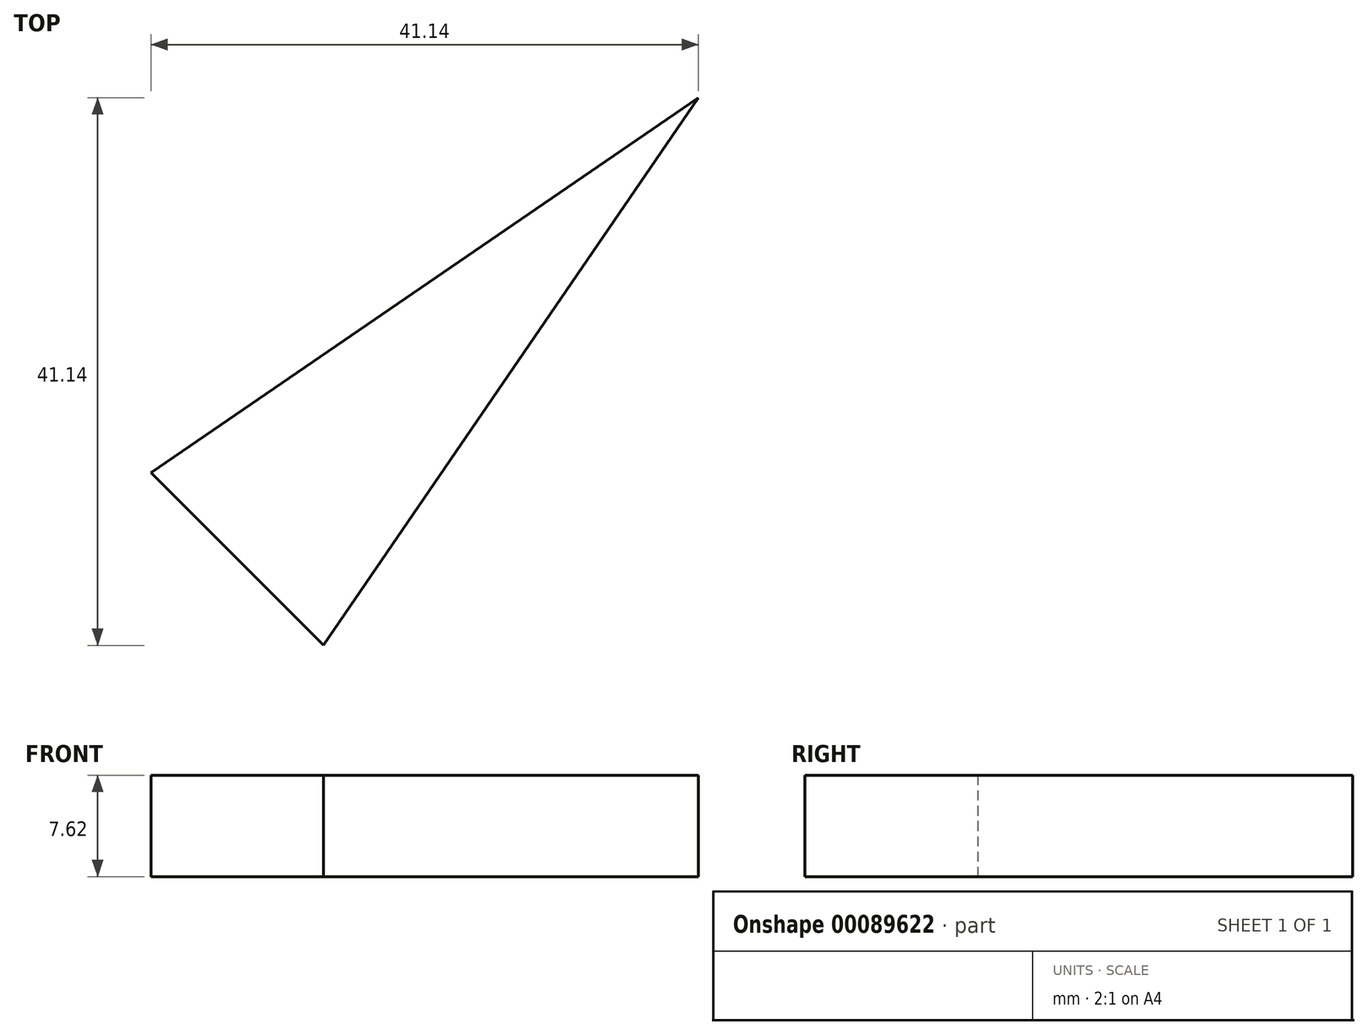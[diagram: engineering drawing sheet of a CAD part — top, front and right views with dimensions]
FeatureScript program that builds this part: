
annotation { "Feature Type Name" : "Feature", "Feature Type Description" : "" }
export const myFeature = defineFeature(function(context is Context, id is Id, definition is map)
    precondition{}
    {
        {
            var Q0;
            Q0=qCreatedBy(makeId("Top.planeOp"),FACE);
            var sketch = newSketch(context, id + "F0", { "sketchPlane" : qUnion([Q0])});
            skCircle(sketch, "E0", {"center": v(0, 0) * mm, "radius": 21.64 * mm});
            skLineSegment(sketch, "E1", {"start": v(0, 21.64) * mm, "end": v(0, -21.64) * mm});
            skLineSegment(sketch, "E2", {"start": v(0, 68.6) * mm, "end": v(0, 22.42) * mm});
            skLineSegment(sketch, "E3", {"start": v(0, 68.6) * mm, "end": v(-9.17, 19.6) * mm});
            skLineSegment(sketch, "E4", {"start": v(-9.17, 19.6) * mm, "end": v(0, 68.6) * mm});
            skLineSegment(sketch, "E5", {"start": v(9.17, 19.6) * mm, "end": v(0, 68.6) * mm});
            skLineSegment(sketch, "E6", {"start": v(-9.17, 19.6) * mm, "end": v(9.17, 19.6) * mm});
            skLineSegment(sketch, "E7", {"start": v(37.42, 47.55) * mm, "end": v(37.42, 1.37) * mm});
            skLineSegment(sketch, "E8", {"start": v(28.25, -1.45) * mm, "end": v(37.42, 47.55) * mm});
            skLineSegment(sketch, "E9", {"start": v(46.59, -1.45) * mm, "end": v(37.42, 47.55) * mm});
            skLineSegment(sketch, "E10", {"start": v(28.25, -1.45) * mm, "end": v(46.59, -1.45) * mm});
            skSolve(sketch);
        }
        {
            var Q0;
            {var subQ0=sQuery(id+"F0.wireOp",EDGE,"E1");var subQ1=sQuery(id+"F0.wireOp",EDGE,"E0");var subQ2=makeQuery(id+"F0.imprint","INTERSECT",VERTEX,{"disambiguationData":[OD(1.0)],"derivedFrom":[subQ1,subQ0]});Q0=makeQuery(id+"F0.imprint","IMPRINT",FACE,{"disambiguationData":[TD([[makeQuery(id+"F0.imprint","IMPRINT",EDGE,{"disambiguationData":[TD([[subQ2,1.0]])],"derivedFrom":subQ0}),1.0]])]});}
            var Q1;
            Q1=makeQuery(id+"F0.imprint","IMPRINT",FACE,{"disambiguationData":[TD([[makeQuery(id+"F0.imprint","IMPRINT",EDGE,{"derivedFrom":sQuery(id+"F0.wireOp",EDGE,"E8")}),-1.0]])]});
            var Q2;
            {var subQ0=sQuery(id+"F0.wireOp",EDGE,"E1");var subQ1=sQuery(id+"F0.wireOp",EDGE,"E0");var subQ2=makeQuery(id+"F0.imprint","INTERSECT",VERTEX,{"disambiguationData":[OD(1.0)],"derivedFrom":[subQ1,subQ0]});Q2=makeQuery(id+"F0.imprint","IMPRINT",FACE,{"disambiguationData":[TD([[makeQuery(id+"F0.imprint","IMPRINT",EDGE,{"disambiguationData":[TD([[subQ2,1.0]])],"derivedFrom":subQ0}),-1.0]])]});}
            var Q3;
            {var subQ0=sQuery(id+"F0.wireOp",EDGE,"E1");var subQ1=sQuery(id+"F0.wireOp",EDGE,"E0");var subQ2=makeQuery(id+"F0.imprint","INTERSECT",VERTEX,{"disambiguationData":[OD(0.0)],"derivedFrom":[subQ1,subQ0]});Q3=makeQuery(id+"F0.imprint","IMPRINT",FACE,{"disambiguationData":[TD([[makeQuery(id+"F0.imprint","IMPRINT",EDGE,{"disambiguationData":[TD([[subQ2,-1.0]])],"derivedFrom":subQ0}),-1.0]])]});}
            var Q4;
            {var subQ0=sQuery(id+"F0.wireOp",EDGE,"E1");var subQ1=sQuery(id+"F0.wireOp",EDGE,"E0");var subQ2=makeQuery(id+"F0.imprint","INTERSECT",VERTEX,{"disambiguationData":[OD(0.0)],"derivedFrom":[subQ1,subQ0]});Q4=makeQuery(id+"F0.imprint","IMPRINT",FACE,{"disambiguationData":[TD([[makeQuery(id+"F0.imprint","IMPRINT",EDGE,{"disambiguationData":[TD([[subQ2,-1.0]])],"derivedFrom":subQ0}),1.0]])]});}
            var Q5;
            {var subQ4=sQuery(id+"F0.wireOp",EDGE,"E4");Q5=makeQuery(id+"F0.imprint","IMPRINT",FACE,{"disambiguationData":[TD([[makeQuery(id+"F0.imprint","IMPRINT",EDGE,{"derivedFrom":subQ4}),-1.0]])]});}
            extrude(context, id + "F1", {"entities" : qUnion([Q0, Q1, Q2, Q3, Q4, Q5]), "depth" : 7.62 * mm});
        }
        {
            var Q0;
            Q0=qCreatedBy(makeId("Front.planeOp"),FACE);
            var sketch = newSketch(context, id + "F2", { "sketchPlane" : qUnion([Q0])});
            skLineSegment(sketch, "E11", {"start": v(28.3, 0) * mm, "end": v(28.3, 31.17) * mm});
            skSolve(sketch);
        }
        {
            var Q0;
            Q0=makeQuery(id+"F1.opExtrude","SWEPT_BODY",BODY,{"disambiguationData":[OSD([sQuery(id+"F0.wireOp",EDGE,"E8"),sQuery(id+"F0.wireOp",EDGE,"E9"),sQuery(id+"F0.wireOp",EDGE,"E10")])]});
            var Q1;
            Q1=sQuery(id+"F2.wireOp",EDGE,"E11");
            transform(context, id + "F3", {"entities" : qUnion([Q0]), "transformType" : TransformType.ROTATION, "transformAxis" : qUnion([Q1]), "angle" : 45 * degree, "oppositeDirection" : true, "makeCopy" : false});
        }
        {
            var Q0;
            Q0=makeQuery(id+"F1.opExtrude","SWEPT_BODY",BODY,{"disambiguationData":[OSD([sQuery(id+"F0.wireOp",EDGE,"E8"),sQuery(id+"F0.wireOp",EDGE,"E9"),sQuery(id+"F0.wireOp",EDGE,"E10")])]});
            transform(context, id + "F4", {"entities" : qUnion([Q0]), "transformType" : TransformType.TRANSLATION_3D, "dx" : -18.06 * mm, "dy" : 20.6 * mm, "dz" : 0 * mm, "makeCopy" : false});
        }
    });
